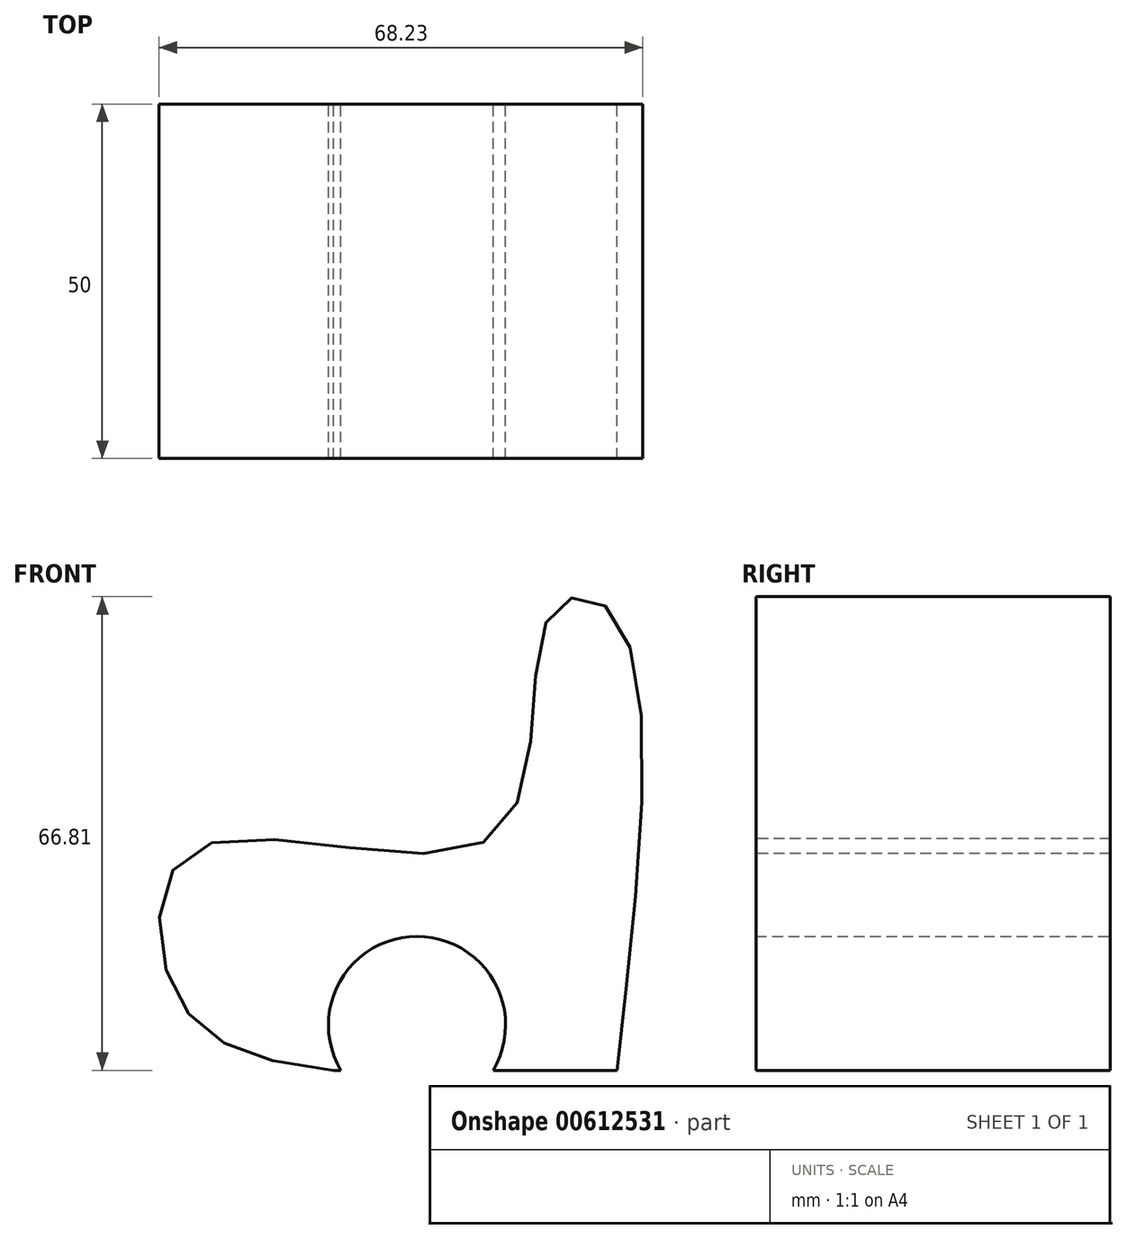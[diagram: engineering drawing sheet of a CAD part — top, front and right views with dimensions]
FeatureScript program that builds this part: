
annotation { "Feature Type Name" : "Feature", "Feature Type Description" : "" }
export const myFeature = defineFeature(function(context is Context, id is Id, definition is map)
    precondition{}
    {
        {
            var Q0;
            Q0=qCreatedBy(makeId("Front.planeOp"),FACE);
            cPlane(context, id + "F0", {"entities" : qUnion([Q0]), "cplaneType" : CPlaneType.OFFSET, "offset" : 25 * mm, "width" : 152.4 * mm, "height" : 152.4 * mm});
        }
        {
            var Q0;
            Q0=qCreatedBy(makeId("Front.planeOp"),FACE);
            var sketch = newSketch(context, id + "F1", { "sketchPlane" : qUnion([Q0])});
            skFitSpline(sketch, "E0", {"points": [v(-39.97, 0) * mm, v(-62.22, 10.76) * mm, v(-59.28, 31.32) * mm, v(-17.29, 33.15) * mm, v(-9.37, 64.41) * mm, v(0, 63.73) * mm, v(0, 0) * mm], "startDerivative": vector(-219.36, 22.63) * mm, "endDerivative": vector(-24.81, -235.6) * mm});
            skLineSegment(sketch, "E1", {"start": v(-39.97, 0) * mm, "end": v(0, 0) * mm});
            skSolve(sketch);
        }
        {
            var Q0;
            Q0=makeQuery(id+"F1.imprint","IMPRINT",FACE,{"disambiguationData":[TD([[makeQuery(id+"F1.imprint","IMPRINT",EDGE,{"derivedFrom":sQuery(id+"F1.wireOp",EDGE,"E0")}),-1.0]])]});
            extrude(context, id + "F2", {"entities" : qUnion([Q0]), "depth" : 50 * mm, "offsetDistance" : 25 * mm});
        }
        {
            var Q0;
            Q0=qCreatedBy(makeId("Front.planeOp"),FACE);
            var sketch = newSketch(context, id + "F3", { "sketchPlane" : qUnion([Q0])});
            skCircle(sketch, "E2", {"center": v(-28.2, 6.4) * mm, "radius": 11.1 * mm});
            skSolve(sketch);
        }
        {
            var Q0;
            Q0=sQuery(id+"F3.wireOp",VERTEX,"E2.center");
            var Q1;
            Q1=makeQuery(id+"F2.opExtrude","SWEPT_BODY",BODY,{"disambiguationData":[OSD([sQuery(id+"F1.wireOp",EDGE,"E0"),sQuery(id+"F1.wireOp",EDGE,"E1")])]});
            hole(context, id + "F4", {"style" : HoleStyle.SIMPLE, "endStyle" : HoleEndStyle.THROUGH, "oppositeDirection" : true, "holeDiameter" : 25 * mm, "majorDiameter" : 5 * mm, "isTappedThrough" : true, "tappedDepth" : 12 * mm, "tapClearance" : 3, "locations" : qUnion([Q0]), "scope" : qUnion([Q1])});
        }
        {
            var Q0;
            Q0=qCreatedBy(makeId("Front.planeOp"),FACE);
            var sketch = newSketch(context, id + "F5", { "sketchPlane" : qUnion([Q0])});
            skFitSpline(sketch, "E3", {"points": [v(-8.36, 49.9) * mm, v(-42.16, 45.58) * mm, v(-60.5, 28.86) * mm], "startDerivative": vector(-68.8, -0.36) * mm, "endDerivative": vector(-34.57, -42.83) * mm});
            skSolve(sketch);
        }
        {
            var Q0;
            Q0=sQuery(id+"F5.wireOp",EDGE,"E3");
            extrude(context, id + "F6", {"bodyType" : ToolBodyType.SURFACE, "surfaceEntities" : qUnion([Q0]), "depth" : 5 * mm, "offsetDistance" : 25 * mm});
        }
        {
            var Q0;
            Q0=makeQuery(id+"F6.opExtrude","SWEPT_BODY",BODY,{"disambiguationData":[OSD([sQuery(id+"F5.wireOp",EDGE,"E3")])]});
            var Q1;
            Q1=qCreatedBy(id+"F0.planeOp",FACE);
            mirror(context, id + "F7", {"entities" : qUnion([Q0]), "mirrorPlane" : qUnion([Q1])});
        }
    });
